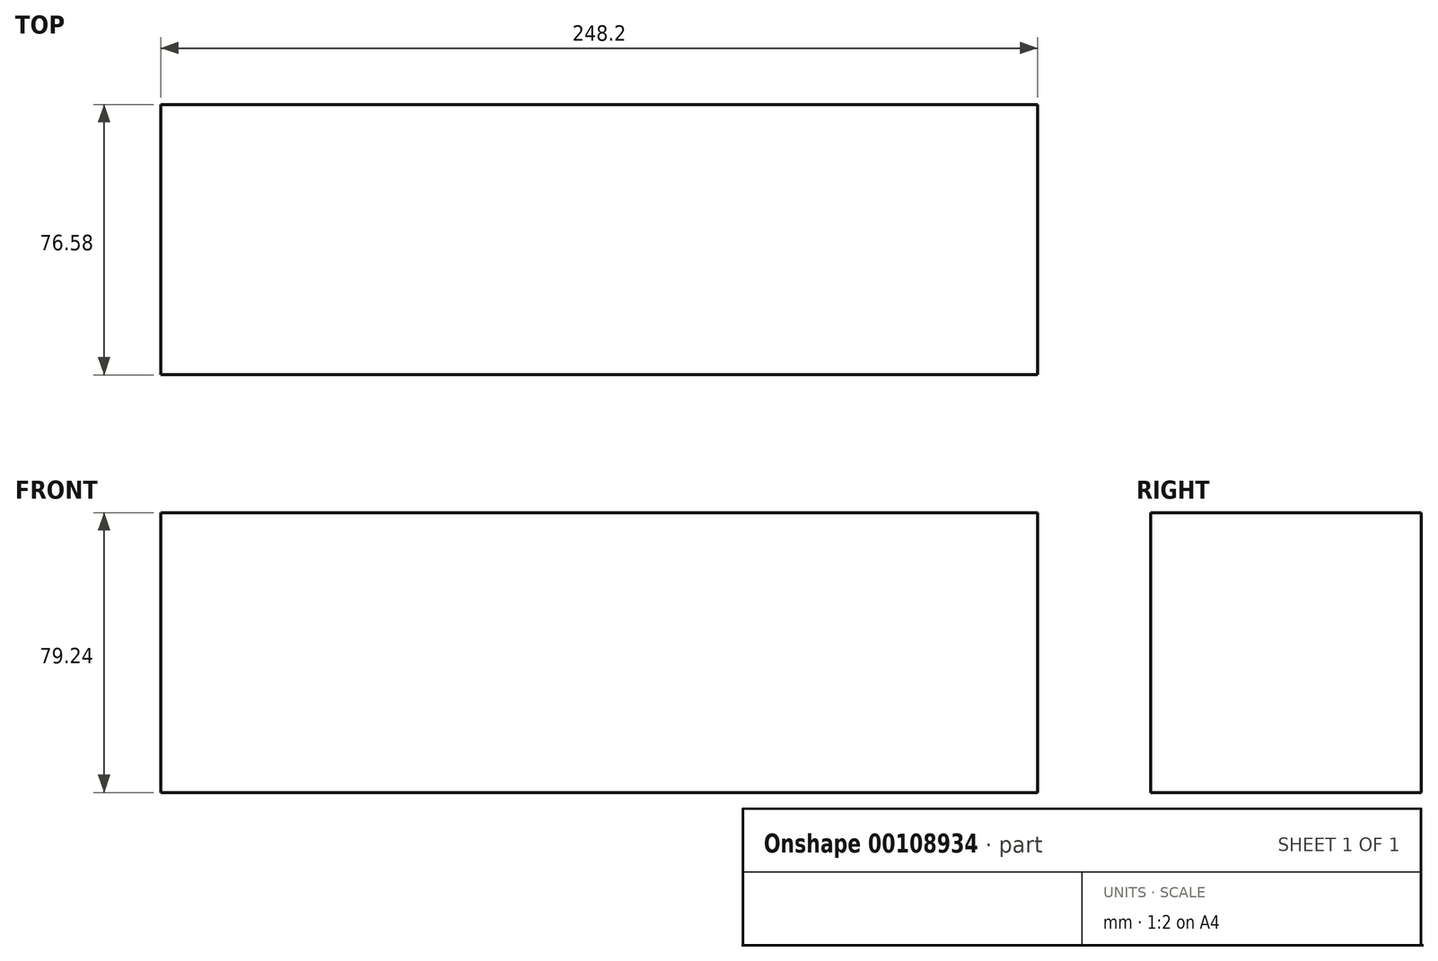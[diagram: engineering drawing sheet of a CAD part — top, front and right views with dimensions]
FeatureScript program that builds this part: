
annotation { "Feature Type Name" : "Feature", "Feature Type Description" : "" }
export const myFeature = defineFeature(function(context is Context, id is Id, definition is map)
    precondition{}
    {
        {
            var Q0;
            Q0=qCreatedBy(makeId("Top.planeOp"),FACE);
            var sketch = newSketch(context, id + "F0", { "sketchPlane" : qUnion([Q0])});
            skLineSegment(sketch, "E0.bottom", {"start": v(124.1, -38.29) * mm, "end": v(-124.1, -38.29) * mm});
            skLineSegment(sketch, "E0.top", {"start": v(124.1, 38.29) * mm, "end": v(-124.1, 38.29) * mm});
            skLineSegment(sketch, "E0.left", {"start": v(124.1, -38.29) * mm, "end": v(124.1, 38.29) * mm});
            skLineSegment(sketch, "E0.right", {"start": v(-124.1, -38.29) * mm, "end": v(-124.1, 38.29) * mm});
            skPoint(sketch, "E0.middle", {"position": v(0, 0) * mm});
            skSolve(sketch);
        }
        {
            var Q0;
            Q0 = qSketchRegion(id + "F0", true);
            extrude(context, id + "F1", {"entities" : qUnion([Q0]), "depth" : 79.24 * mm});
        }
    });
